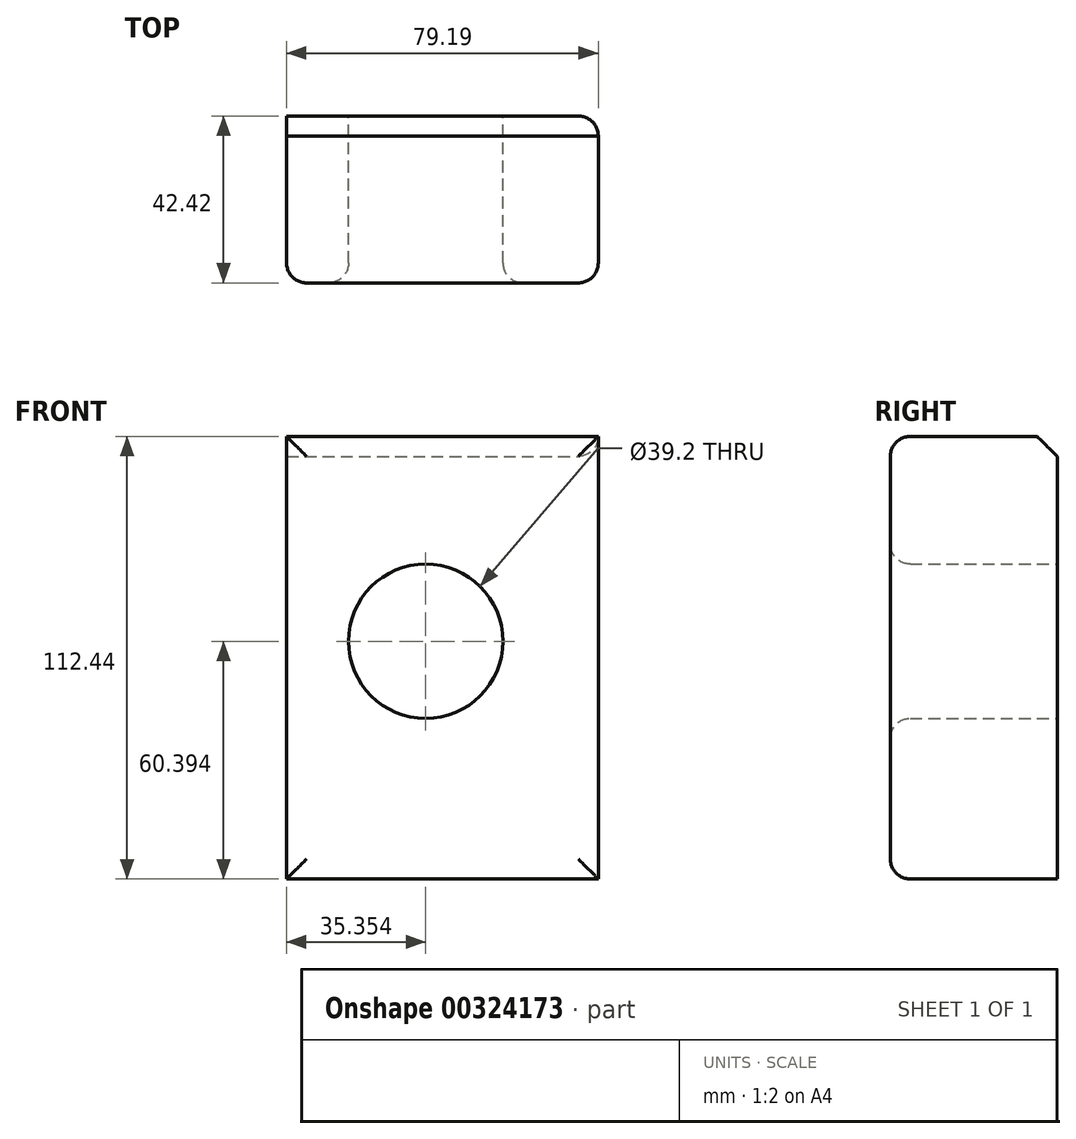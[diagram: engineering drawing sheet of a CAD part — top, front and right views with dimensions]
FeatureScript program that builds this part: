
annotation { "Feature Type Name" : "Feature", "Feature Type Description" : "" }
export const myFeature = defineFeature(function(context is Context, id is Id, definition is map)
    precondition{}
    {
        {
            var Q0;
            Q0=qCreatedBy(makeId("Front.planeOp"),FACE);
            var sketch = newSketch(context, id + "F0", { "sketchPlane" : qUnion([Q0])});
            skLineSegment(sketch, "E0.bottom", {"start": v(-222.66, 65.34) * mm, "end": v(-143.47, 65.34) * mm});
            skLineSegment(sketch, "E0.top", {"start": v(-222.66, -47.1) * mm, "end": v(-143.47, -47.1) * mm});
            skLineSegment(sketch, "E0.left", {"start": v(-222.66, 65.34) * mm, "end": v(-222.66, -47.1) * mm});
            skLineSegment(sketch, "E0.right", {"start": v(-143.47, 65.34) * mm, "end": v(-143.47, -47.1) * mm});
            skCircle(sketch, "E1", {"center": v(-187.3, 13.3) * mm, "radius": 19.6 * mm});
            skSolve(sketch);
        }
        {
            var Q0;
            Q0=makeQuery(id+"F0.imprint","IMPRINT",FACE,{"disambiguationData":[TD([[makeQuery(id+"F0.imprint","IMPRINT",EDGE,{"derivedFrom":sQuery(id+"F0.wireOp",EDGE,"E0.bottom")}),-1.0]])]});
            var Q1;
            Q1=makeQuery(id+"F0.imprint","IMPRINT",FACE,{"disambiguationData":[TD([[makeQuery(id+"F0.imprint","IMPRINT",EDGE,{"derivedFrom":sQuery(id+"F0.wireOp",EDGE,"xOaTgeyj-ymXA-RhSs-WI9p-JCdF8rygd11N")}),1.0]])]});
            extrude(context, id + "F1", {"entities" : qUnion([Q0, Q1]), "endBound" : BoundingType.SYMMETRIC, "depth" : 42.42 * mm});
        }
        {
            var Q0;
            Q0=makeQuery(id+"F1.opExtrude","CAP_FACE",FACE,{"disambiguationData":[OSD([sQuery(id+"F0.wireOp",EDGE,"E0.bottom"),sQuery(id+"F0.wireOp",EDGE,"E0.top"),sQuery(id+"F0.wireOp",EDGE,"E0.left"),sQuery(id+"F0.wireOp",EDGE,"E0.right"),sQuery(id+"F0.wireOp",EDGE,"E1")])],"isStart":false});
            fillet(context, id + "F2", {"entities" : qUnion([Q0]), "radius" : 5.08 * mm, "tangentPropagation" : true, "allowEdgeOverflow" : false});
        }
        {
            var Q0;
            Q0=makeQuery(id+"F1.opExtrude","CAP_EDGE",EDGE,{"disambiguationData":[OSD([sQuery(id+"F0.wireOp",EDGE,"E0.bottom")])],"isStart":true});
            chamfer(context, id + "F3", {"entities" : qUnion([Q0]), "width" : 5.08 * mm, "tangentPropagation" : true});
        }
        {
            var Q0;
            Q0=makeQuery(id+"F1.opExtrude","CAP_EDGE",EDGE,{"disambiguationData":[OSD([sQuery(id+"F0.wireOp",EDGE,"E0.right")])],"isStart":true});
            fillet(context, id + "F4", {"entities" : qUnion([Q0]), "radius" : 5.08 * mm, "tangentPropagation" : true, "allowEdgeOverflow" : false});
        }
    });
